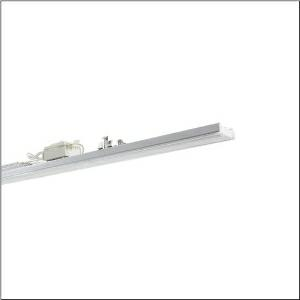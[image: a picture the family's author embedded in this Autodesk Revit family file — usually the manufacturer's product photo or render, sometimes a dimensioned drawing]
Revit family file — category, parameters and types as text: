
# Revit family: licross_21_recessed_mo_52tl117n485g
name_source: partatom
category: Lighting Fixtures
units: mm (PartAtom-declared; Revit-internal decimal feet)

## family parameters
Cut with Voids When Loaded = No
Host = Face
Light Source = No
Part Type = Normal
Room Calculation Point = No
Round Connector Dimension = Use Diameter
Shared = No

## types (1)
- Licross 21 Recessed MO (1 x LED, 8680 lm, 47.9 W, 4000K)
    Apparent Load = 48 VA
    CIE Flux Codes = 89 96 99 100 100
    Color Rendering = 80
    Color Temperature = 4000K
    Default Elevation = 1800 mm
    Description = Licross 21 Recessed MO, luminaire insert, of sheet steel, galvanised, coil coated, white, length: 1.500mm, width: 66mm, height: 67mm, LED rated luminous flux: 8.680lm, light colour: 840, SDCM (Standard Deviation of Colour Matching)MacAdam ≤ 3 SDCM (initial), control gear: ON/OFF, with plug, 3-pole, with phase selection, mains connection: 220..240V, AC, 50/60Hz, rated input power: 48W, internal wiring halogen-free, primary light control with lens, of plastic, primary optical cover: cover, of PMMA, light emission: direct distribution, primary light characteristic: symmetric, protection rating (complete): IP40, insulation class (complete): insulation class I (protective earthing), certification: CE, ENEC, VDE, UKCA, protection symbol: D if used in an environment without relevant dust loads with corresponding accessories, impact resistance: IK06, permissible ambient temperature for indoor applications: -35..+40°C, corresponds to IFS (International Featured Standards) requirements for safety and quality in the food industry, reducing of maximum allowable ambient temperature of 5°C with ceiling mounting, LABS conformity tested according to VDMA 24364:2018-05, The light source and the operating device comply with the requirements of the Ecodesign Regulation (EU) 2019/2020 and are replaceable in accordance with this regulation, packaging unit: 1 piece
    Height = 58 mm
    Lamp = 1 x LED
    Lamp Light Flux = 8680 lm
    Lamp Power = 47.9 W
    Lamp count = 1
    Length = 1500 mm
    Luminous efficacy = 181 lm/W
    Manufacturer = Siteco
    ModVariant = No
    Model = 52TL117N485G
    Mounting Place = Ceiling
    Mounting Type = Pendant
    Number of Poles = 1
    OnlyDefault = Yes
    Power Factor = 1
    Product Name = Licross 21 Recessed MO
    Product group = luminaire insert | ceiling pendant
    ProductGroupID = 901
    Protection Class = Protection class I
    Protection Degree = IP 40
    RLX_Detail_Level = 1
    RLX_Emergency_Light_Flux = 0 lm
    RLX_Emergency_Type = 0
    RLX_Emergency_Type_DB = No
    RlxData = <blob elided: 21177 chars, md5=2625fd37>
    Socket = socket
    Standby Power = 0 W
    System Light Flux = 8680 lm
    System Power = 48 W
    Type Comments = Product without accessories
    Type Image = l_1296930.jpg
    URL = http://relux.com
    VarID = ---
    Voltage = 0 V
    Weight = 0.00 kg
    Width = 66 mm

## geometry (parser evidence)
native form markers: Blend x4, Sweep x10
no freeform markers — native parametric forms only
